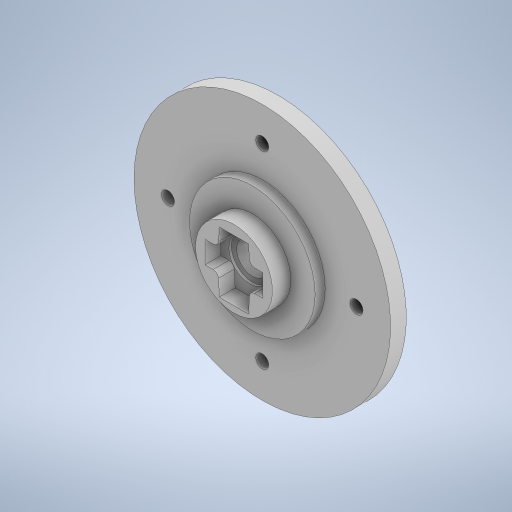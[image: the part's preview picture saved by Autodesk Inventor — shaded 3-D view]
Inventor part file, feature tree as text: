
AUTODESK INVENTOR PART (.ipt)
format: ipt  version: 2023.1 (Build 271208000, 208)  size: 599,040 bytes
history: native  units: mm
features: sketch x18, extrude x18, projected_geometry x7, fillet x2, other x1
ambient origin geometry x8: Origin, YZ Plane, XZ Plane, XY Plane, X Axis, Y Axis, Z Axis, Center Point
bodies: Body1 (feature_tree)
feature tree (46):
  other  "솔리드1"
  sketch  "스케치1"
  extrude  "돌출1"  Depth=5.0mm
  extrude  "돌출2"  Depth=1.9mm
  extrude  "돌출3"  Depth=16.5mm
  extrude  "돌출4"  Depth=29.0mm
  extrude  "돌출5"  Depth=1.0mm
  sketch  "스케치4"
  extrude  "돌출6"  Depth=1.0mm
  extrude  "돌출7"  Depth=1.0mm
  extrude  "돌출8"  Depth=1.0mm
  extrude  "돌출9"  Depth=10.0mm
  extrude  "돌출10"  Depth=10.0mm
  fillet  "모깎기1"  Radius=16.6mm
  sketch  "스케치11"
  extrude  "돌출11"  Depth=14.0mm
  sketch  "스케치14"
  extrude  "돌출12"  Depth=4.0mm
  extrude  "돌출13"  Depth=4.0mm
  extrude  "돌출14"  Depth=6.8mm
  extrude  "돌출15"  Depth=10.0mm
  fillet  "모깎기2"  Radius=4.7mm
  extrude  "돌출16"  Depth=10.0mm
  extrude  "돌출17"  Depth=10.0mm
  extrude  "돌출18"  Depth=2.2mm TaperAngle=0.0deg
  sketch  "스케치2"
  sketch  "스케치3"
  sketch  "스케치5"
  sketch  "스케치6"
  sketch  "스케치7"
  sketch  "스케치9"
  sketch  "스케치10"
  sketch  "스케치12"
  projected_geometry  "투영된 루프1"
  projected_geometry  "투영된 루프2"
  projected_geometry  "투영된 루프3"
  projected_geometry  "투영된 루프4"
  projected_geometry  "투영된 루프5"
  projected_geometry  "투영된 루프6"
  sketch  "스케치15"
  sketch  "스케치16"
  sketch  "스케치17"
  projected_geometry  "투영된 루프7"
  sketch  "스케치18"
  sketch  "스케치19"
  sketch  "스케치20"
